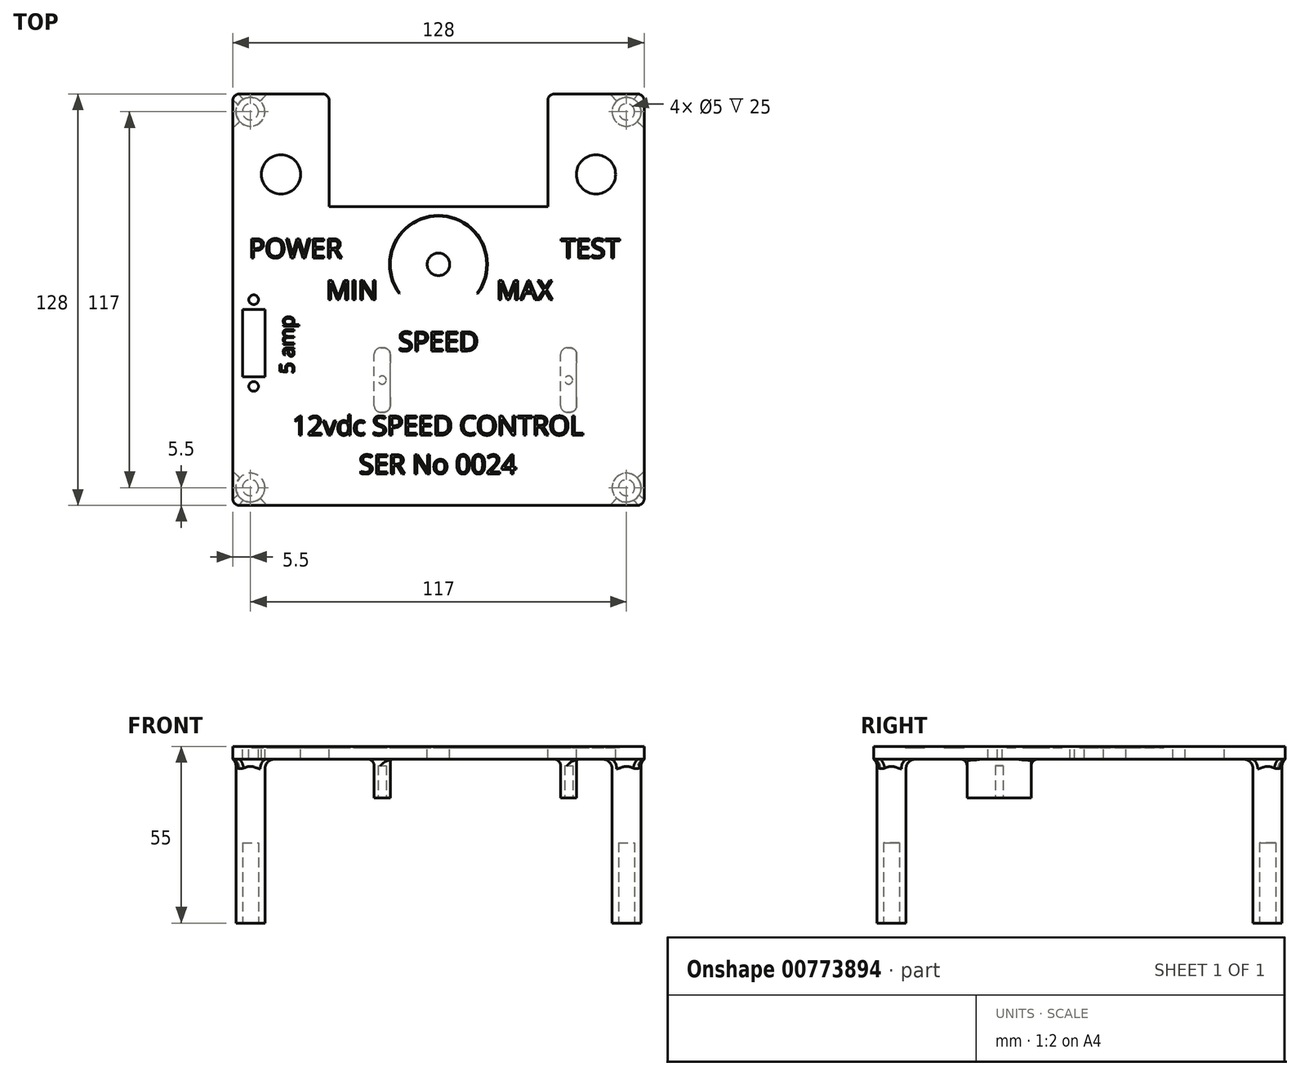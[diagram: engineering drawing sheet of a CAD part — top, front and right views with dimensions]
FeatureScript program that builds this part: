
annotation { "Feature Type Name" : "Feature", "Feature Type Description" : "" }
export const myFeature = defineFeature(function(context is Context, id is Id, definition is map)
    precondition{}
    {
        {
            var Q0;
            Q0=qCreatedBy(makeId("Top.planeOp"),FACE);
            var sketch = newSketch(context, id + "F0", { "sketchPlane" : qUnion([Q0])});
            skLineSegment(sketch, "E0.bottom", {"start": v(0, 0) * mm, "end": v(128, 0) * mm});
            skLineSegment(sketch, "E0.top", {"start": v(0, 128) * mm, "end": v(30, 128) * mm});
            skLineSegment(sketch, "E0.left", {"start": v(0, 0) * mm, "end": v(0, 128) * mm});
            skLineSegment(sketch, "E0.right", {"start": v(128, 0) * mm, "end": v(128, 128) * mm});
            skLineSegment(sketch, "E1", {"start": v(30, 128) * mm, "end": v(30, 93) * mm});
            skLineSegment(sketch, "E2", {"start": v(98, 93) * mm, "end": v(98, 128) * mm});
            skLineSegment(sketch, "E3", {"start": v(98, 93) * mm, "end": v(30, 93) * mm});
            skCircle(sketch, "E4", {"center": v(15, 103) * mm, "radius": 6.1 * mm});
            skCircle(sketch, "E5", {"center": v(113, 103) * mm, "radius": 6.1 * mm});
            skCircle(sketch, "E6", {"center": v(64, 75) * mm, "radius": 3.5 * mm});
            skLineSegment(sketch, "E7.bottom", {"start": v(3, 61) * mm, "end": v(10, 61) * mm});
            skLineSegment(sketch, "E7.top", {"start": v(3, 40) * mm, "end": v(10, 40) * mm});
            skLineSegment(sketch, "E7.left", {"start": v(3, 61) * mm, "end": v(3, 40) * mm});
            skLineSegment(sketch, "E7.right", {"start": v(10, 61) * mm, "end": v(10, 40) * mm});
            skLineSegment(sketch, "E8.trimOffspring", {"start": v(98, 128) * mm, "end": v(128, 128) * mm});
            skCircle(sketch, "E9", {"center": v(6.5, 64) * mm, "radius": 1.5 * mm});
            skPoint(sketch, "E9.centerSnap0", {"position": v(6.5, 61) * mm});
            skCircle(sketch, "E10", {"center": v(6.5, 37) * mm, "radius": 1.5 * mm});
            skPoint(sketch, "E10.centerSnap0", {"position": v(6.5, 40) * mm});
            skSolve(sketch);
        }
        {
            var Q0;
            Q0=makeQuery(id+"F0.imprint","IMPRINT",FACE,{"disambiguationData":[TD([[makeQuery(id+"F0.imprint","IMPRINT",EDGE,{"derivedFrom":sQuery(id+"F0.wireOp",EDGE,"E0.bottom")}),1.0]])]});
            extrude(context, id + "F1", {"entities" : qUnion([Q0]), "oppositeDirection" : true, "depth" : 4 * mm, "offsetDistance" : 25 * mm});
        }
        {
            var Q0;
            Q0=qCreatedBy(makeId("Top.planeOp"),FACE);
            var sketch = newSketch(context, id + "F2", { "sketchPlane" : qUnion([Q0])});
            skText(sketch, "E11", { "text": "SPEED", "fontName": "OpenSans-Regular.ttf"});
            skText(sketch, "E12", { "text": "POWER", "fontName": "OpenSans-Regular.ttf"});
            skText(sketch, "E13", { "text": "TEST", "fontName": "OpenSans-Regular.ttf"});
            skText(sketch, "E14", { "text": "MIN", "fontName": "OpenSans-Regular.ttf"});
            skText(sketch, "E15", { "text": "MAX", "fontName": "OpenSans-Regular.ttf"});
            skText(sketch, "E16", { "text": "5 amp\n", "fontName": "OpenSans-Regular.ttf"});
            skText(sketch, "E17", { "text": "12vdc SPEED CONTROL", "fontName": "OpenSans-Regular.ttf"});
            skArc(sketch, "E18", {"start": v(76, 66) * mm, "mid": v(64, 90) * mm, "end": v(52, 66) * mm});
            skArc(sketch, "E19", {"start": v(76.2, 65.86) * mm, "mid": v(64, 90.25) * mm, "end": v(51.8, 65.85) * mm});
            skLineSegment(sketch, "E20", {"start": v(52, 66) * mm, "end": v(51.8, 65.85) * mm});
            skLineSegment(sketch, "E21", {"start": v(76, 66) * mm, "end": v(76.2, 65.86) * mm});
            skText(sketch, "E22", { "text": "SER No 0024", "fontName": "OpenSans-Regular.ttf"});
            const initialGuessF2  = {"E11": [0.05152, 0.04806, 1, 0, 0.006], "E12": [0.005, 0.077, 1, 0, 0.006], "E13": [0.1021, 0.077, 1, 0, 0.006], "E14": [0.02907, 0.064, 1, 0, 0.006], "E15": [0.08194, 0.064, 1, 0, 0.006], "E16": [0.01905, 0.04095, 0, 1, 0.00444], "E17": [0.0185, 0.02184, 1, 0, 0.006], "E22": [0.03928, 0.0098, 1, 0, 0.006]};
            skSetInitialGuess(sketch, initialGuessF2);
            skSolve(sketch);
        }
        {
            var Q0;
            Q0 = qSketchRegion(id + "F2", true);
            extrude(context, id + "F3", {"entities" : qUnion([Q0]), "operationType" : NewBodyOperationType.REMOVE, "oppositeDirection" : true, "depth" : .5 * mm, "offsetDistance" : 25 * mm});
        }
        {
            var Q0;
            Q0=qCreatedBy(makeId("Top.planeOp"),FACE);
            var sketch = newSketch(context, id + "F4", { "sketchPlane" : qUnion([Q0])});
            skCircle(sketch, "E23", {"center": v(5.5, 122.5) * mm, "radius": 4.5 * mm});
            skCircle(sketch, "E24.1.0.0", {"center": v(122.5, 122.5) * mm, "radius": 4.5 * mm});
            skLineSegment(sketch, "E24.direction1", {"start": v(5.5, 122.5) * mm, "end": v(122.5, 122.5) * mm, "construction": true});
            skCircle(sketch, "E25", {"center": v(5.5, 5.5) * mm, "radius": 4.5 * mm});
            skCircle(sketch, "E26", {"center": v(122.5, 5.5) * mm, "radius": 4.5 * mm});
            skSolve(sketch);
        }
        {
            var Q0;
            Q0 = qSketchRegion(id + "F4", true);
            extrude(context, id + "F5", {"entities" : qUnion([Q0]), "operationType" : NewBodyOperationType.ADD, "oppositeDirection" : true, "depth" : 55 * mm, "offsetDistance" : 25 * mm});
        }
        {
            var Q0;
            Q0=makeQuery(id+"F5.opExtrude","CAP_FACE",FACE,{"disambiguationData":[OSD([sQuery(id+"F4.wireOp",EDGE,"E25")])],"isStart":false});
            var sketch = newSketch(context, id + "F6", { "sketchPlane" : qUnion([Q0])});
            skCircle(sketch, "E27", {"center": v(5.5, -5.5) * mm, "radius": 2.5 * mm});
            skCircle(sketch, "E28.0.1.0", {"center": v(5.5, -122.5) * mm, "radius": 2.5 * mm});
            skCircle(sketch, "E28.1.0.0", {"center": v(122.5, -5.5) * mm, "radius": 2.5 * mm});
            skCircle(sketch, "E28.1.1.0", {"center": v(122.5, -122.5) * mm, "radius": 2.5 * mm});
            skLineSegment(sketch, "E28.direction1", {"start": v(5.5, -5.5) * mm, "end": v(122.5, -5.5) * mm, "construction": true});
            skLineSegment(sketch, "E28.direction2", {"start": v(5.5, -5.5) * mm, "end": v(5.5, -122.5) * mm, "construction": true});
            skSolve(sketch);
        }
        {
            var Q0;
            Q0 = qSketchRegion(id + "F6", true);
            extrude(context, id + "F7", {"entities" : qUnion([Q0]), "operationType" : NewBodyOperationType.REMOVE, "oppositeDirection" : true, "depth" : 25 * mm, "offsetDistance" : 25 * mm});
        }
        {
            var Q0;
            Q0=makeQuery(id+"F1.opExtrude","SWEPT_EDGE",EDGE,{"disambiguationData":[OSD([sQuery(id+"F0.wireOp",EDGE,"E0.top"),sQuery(id+"F0.wireOp",EDGE,"E0.left")])]});
            var Q1;
            Q1=makeQuery(id+"F1.opExtrude","SWEPT_EDGE",EDGE,{"disambiguationData":[OSD([sQuery(id+"F0.wireOp",EDGE,"E0.right"),sQuery(id+"F0.wireOp",EDGE,"E8.trimOffspring")])]});
            var Q2;
            Q2=makeQuery(id+"F1.opExtrude","SWEPT_EDGE",EDGE,{"disambiguationData":[OSD([sQuery(id+"F0.wireOp",EDGE,"E0.bottom"),sQuery(id+"F0.wireOp",EDGE,"E0.right")])]});
            var Q3;
            Q3=makeQuery(id+"F1.opExtrude","SWEPT_EDGE",EDGE,{"disambiguationData":[OSD([sQuery(id+"F0.wireOp",EDGE,"E0.bottom"),sQuery(id+"F0.wireOp",EDGE,"E0.left")])]});
            var Q4;
            Q4=makeQuery(id+"F1.opExtrude","SWEPT_EDGE",EDGE,{"disambiguationData":[OSD([sQuery(id+"F0.wireOp",EDGE,"E0.top"),sQuery(id+"F0.wireOp",EDGE,"E1")])]});
            var Q5;
            Q5=makeQuery(id+"F1.opExtrude","SWEPT_EDGE",EDGE,{"disambiguationData":[OSD([sQuery(id+"F0.wireOp",EDGE,"E2"),sQuery(id+"F0.wireOp",EDGE,"E8.trimOffspring")])]});
            fillet(context, id + "F8", {"entities" : qUnion([Q0, Q1, Q2, Q3, Q4, Q5]), "radius" : 2 * mm, "tangentPropagation" : true, "allowEdgeOverflow" : false});
        }
        {
            var Q0;
            Q0=qCreatedBy(makeId("Top.planeOp"),FACE);
            var sketch = newSketch(context, id + "F9", { "sketchPlane" : qUnion([Q0])});
            skLineSegment(sketch, "E29.bottom", {"start": v(102, 29) * mm, "end": v(107, 29) * mm});
            skLineSegment(sketch, "E29.top", {"start": v(102, 49) * mm, "end": v(107, 49) * mm});
            skLineSegment(sketch, "E29.left", {"start": v(102, 29) * mm, "end": v(102, 49) * mm});
            skLineSegment(sketch, "E29.right", {"start": v(107, 29) * mm, "end": v(107, 49) * mm});
            skPoint(sketch, "E30.oppositeSnap0", {"position": v(104.5, 49) * mm});
            skLineSegment(sketch, "E30.bottom", {"start": v(44, 29) * mm, "end": v(49, 29) * mm});
            skLineSegment(sketch, "E30.top", {"start": v(44, 49) * mm, "end": v(49, 49) * mm});
            skLineSegment(sketch, "E30.left", {"start": v(49, 29) * mm, "end": v(49, 49) * mm});
            skLineSegment(sketch, "E30.right", {"start": v(44, 29) * mm, "end": v(44, 49) * mm});
            skSolve(sketch);
        }
        {
            var Q0;
            Q0 = qSketchRegion(id + "F9", true);
            extrude(context, id + "F10", {"entities" : qUnion([Q0]), "operationType" : NewBodyOperationType.ADD, "oppositeDirection" : true, "depth" : 16 * mm, "offsetDistance" : 25 * mm});
        }
        {
            var Q0;
            Q0=makeQuery(id+"F10.opExtrude","CAP_FACE",FACE,{"disambiguationData":[OSD([sQuery(id+"F9.wireOp",EDGE,"E29.bottom"),sQuery(id+"F9.wireOp",EDGE,"E29.top"),sQuery(id+"F9.wireOp",EDGE,"E29.left"),sQuery(id+"F9.wireOp",EDGE,"E29.right")])],"isStart":false});
            var sketch = newSketch(context, id + "F11", { "sketchPlane" : qUnion([Q0])});
            skCircle(sketch, "E31", {"center": v(104.5, -39) * mm, "radius": 1.25 * mm});
            skCircle(sketch, "E32", {"center": v(46.5, -39) * mm, "radius": 1.25 * mm});
            skPoint(sketch, "E33.orphan", {"position": v(104.5, -29) * mm});
            skPoint(sketch, "E34.orphan", {"position": v(104.5, -49) * mm});
            skSolve(sketch);
        }
        {
            var Q0;
            Q0 = qSketchRegion(id + "F11", true);
            extrude(context, id + "F12", {"entities" : qUnion([Q0]), "operationType" : NewBodyOperationType.REMOVE, "oppositeDirection" : true, "depth" : 10 * mm, "offsetDistance" : 25 * mm});
        }
        {
            var Q0;
            Q0=makeQuery(id+"F10.opExtrude","SWEPT_EDGE",EDGE,{"disambiguationData":[OSD([sQuery(id+"F9.wireOp",EDGE,"E30.bottom"),sQuery(id+"F9.wireOp",EDGE,"E30.left")])]});
            var Q1;
            Q1=makeQuery(id+"F10.opExtrude","SWEPT_EDGE",EDGE,{"disambiguationData":[OSD([sQuery(id+"F9.wireOp",EDGE,"E30.bottom"),sQuery(id+"F9.wireOp",EDGE,"E30.right")])]});
            var Q2;
            Q2=makeQuery(id+"F10.opExtrude","SWEPT_EDGE",EDGE,{"disambiguationData":[OSD([sQuery(id+"F9.wireOp",EDGE,"E29.bottom"),sQuery(id+"F9.wireOp",EDGE,"E29.right")])]});
            var Q3;
            Q3=makeQuery(id+"F10.opExtrude","SWEPT_EDGE",EDGE,{"disambiguationData":[OSD([sQuery(id+"F9.wireOp",EDGE,"E29.top"),sQuery(id+"F9.wireOp",EDGE,"E29.right")])]});
            var Q4;
            Q4=makeQuery(id+"F10.opExtrude","SWEPT_EDGE",EDGE,{"disambiguationData":[OSD([sQuery(id+"F9.wireOp",EDGE,"E29.bottom"),sQuery(id+"F9.wireOp",EDGE,"E29.left")])]});
            var Q5;
            Q5=makeQuery(id+"F10.opExtrude","SWEPT_EDGE",EDGE,{"disambiguationData":[OSD([sQuery(id+"F9.wireOp",EDGE,"E30.top"),sQuery(id+"F9.wireOp",EDGE,"E30.right")])]});
            var Q6;
            Q6=makeQuery(id+"F10.opExtrude","SWEPT_EDGE",EDGE,{"disambiguationData":[OSD([sQuery(id+"F9.wireOp",EDGE,"E29.top"),sQuery(id+"F9.wireOp",EDGE,"E29.left")])]});
            var Q7;
            Q7=makeQuery(id+"F10.opExtrude","SWEPT_EDGE",EDGE,{"disambiguationData":[OSD([sQuery(id+"F9.wireOp",EDGE,"E30.top"),sQuery(id+"F9.wireOp",EDGE,"E30.left")])]});
            var Q8;
            Q8=makeQuery(id+"F10.boolean.opBoolean","INTERSECT",EDGE,{"derivedFrom":[makeQuery(id+"F1.opExtrude","CAP_FACE",FACE,{"disambiguationData":[OSD([sQuery(id+"F0.wireOp",EDGE,"E0.bottom"),sQuery(id+"F0.wireOp",EDGE,"E0.top"),sQuery(id+"F0.wireOp",EDGE,"E0.left"),sQuery(id+"F0.wireOp",EDGE,"E0.right"),sQuery(id+"F0.wireOp",EDGE,"E1"),sQuery(id+"F0.wireOp",EDGE,"E2"),sQuery(id+"F0.wireOp",EDGE,"E3"),sQuery(id+"F0.wireOp",EDGE,"E4"),sQuery(id+"F0.wireOp",EDGE,"E5"),sQuery(id+"F0.wireOp",EDGE,"E6"),sQuery(id+"F0.wireOp",EDGE,"E7.bottom"),sQuery(id+"F0.wireOp",EDGE,"E7.top"),sQuery(id+"F0.wireOp",EDGE,"E7.left"),sQuery(id+"F0.wireOp",EDGE,"E7.right"),sQuery(id+"F0.wireOp",EDGE,"E8.trimOffspring"),sQuery(id+"F0.wireOp",EDGE,"E9"),sQuery(id+"F0.wireOp",EDGE,"E10")])],"isStart":false}),makeQuery(id+"F10.opExtrude","SWEPT_FACE",FACE,{"disambiguationData":[OSD([sQuery(id+"F9.wireOp",EDGE,"E30.right")])]})]});
            var Q9;
            Q9=makeQuery(id+"F10.boolean.opBoolean","INTERSECT",EDGE,{"derivedFrom":[makeQuery(id+"F1.opExtrude","CAP_FACE",FACE,{"disambiguationData":[OSD([sQuery(id+"F0.wireOp",EDGE,"E0.bottom"),sQuery(id+"F0.wireOp",EDGE,"E0.top"),sQuery(id+"F0.wireOp",EDGE,"E0.left"),sQuery(id+"F0.wireOp",EDGE,"E0.right"),sQuery(id+"F0.wireOp",EDGE,"E1"),sQuery(id+"F0.wireOp",EDGE,"E2"),sQuery(id+"F0.wireOp",EDGE,"E3"),sQuery(id+"F0.wireOp",EDGE,"E4"),sQuery(id+"F0.wireOp",EDGE,"E5"),sQuery(id+"F0.wireOp",EDGE,"E6"),sQuery(id+"F0.wireOp",EDGE,"E7.bottom"),sQuery(id+"F0.wireOp",EDGE,"E7.top"),sQuery(id+"F0.wireOp",EDGE,"E7.left"),sQuery(id+"F0.wireOp",EDGE,"E7.right"),sQuery(id+"F0.wireOp",EDGE,"E8.trimOffspring"),sQuery(id+"F0.wireOp",EDGE,"E9"),sQuery(id+"F0.wireOp",EDGE,"E10")])],"isStart":false}),makeQuery(id+"F10.opExtrude","SWEPT_FACE",FACE,{"disambiguationData":[OSD([sQuery(id+"F9.wireOp",EDGE,"E29.left")])]})]});
            fillet(context, id + "F13", {"entities" : qUnion([Q0, Q1, Q2, Q3, Q4, Q5, Q6, Q7, Q8, Q9]), "radius" : 2 * mm, "tangentPropagation" : true, "allowEdgeOverflow" : false});
        }
        {
            var Q0;
            Q0=makeQuery(id+"F5.boolean.opBoolean","INTERSECT",EDGE,{"derivedFrom":[makeQuery(id+"F1.opExtrude","CAP_FACE",FACE,{"disambiguationData":[OSD([sQuery(id+"F0.wireOp",EDGE,"E0.bottom"),sQuery(id+"F0.wireOp",EDGE,"E0.top"),sQuery(id+"F0.wireOp",EDGE,"E0.left"),sQuery(id+"F0.wireOp",EDGE,"E0.right"),sQuery(id+"F0.wireOp",EDGE,"E1"),sQuery(id+"F0.wireOp",EDGE,"E2"),sQuery(id+"F0.wireOp",EDGE,"E3"),sQuery(id+"F0.wireOp",EDGE,"E4"),sQuery(id+"F0.wireOp",EDGE,"E5"),sQuery(id+"F0.wireOp",EDGE,"E6"),sQuery(id+"F0.wireOp",EDGE,"E7.bottom"),sQuery(id+"F0.wireOp",EDGE,"E7.top"),sQuery(id+"F0.wireOp",EDGE,"E7.left"),sQuery(id+"F0.wireOp",EDGE,"E7.right"),sQuery(id+"F0.wireOp",EDGE,"E8.trimOffspring"),sQuery(id+"F0.wireOp",EDGE,"E9"),sQuery(id+"F0.wireOp",EDGE,"E10")])],"isStart":false}),makeQuery(id+"F5.opExtrude","SWEPT_FACE",FACE,{"disambiguationData":[OSD([sQuery(id+"F4.wireOp",EDGE,"E26")])]})]});
            var Q1;
            Q1=makeQuery(id+"F5.boolean.opBoolean","INTERSECT",EDGE,{"derivedFrom":[makeQuery(id+"F1.opExtrude","CAP_FACE",FACE,{"disambiguationData":[OSD([sQuery(id+"F0.wireOp",EDGE,"E0.bottom"),sQuery(id+"F0.wireOp",EDGE,"E0.top"),sQuery(id+"F0.wireOp",EDGE,"E0.left"),sQuery(id+"F0.wireOp",EDGE,"E0.right"),sQuery(id+"F0.wireOp",EDGE,"E1"),sQuery(id+"F0.wireOp",EDGE,"E2"),sQuery(id+"F0.wireOp",EDGE,"E3"),sQuery(id+"F0.wireOp",EDGE,"E4"),sQuery(id+"F0.wireOp",EDGE,"E5"),sQuery(id+"F0.wireOp",EDGE,"E6"),sQuery(id+"F0.wireOp",EDGE,"E7.bottom"),sQuery(id+"F0.wireOp",EDGE,"E7.top"),sQuery(id+"F0.wireOp",EDGE,"E7.left"),sQuery(id+"F0.wireOp",EDGE,"E7.right"),sQuery(id+"F0.wireOp",EDGE,"E8.trimOffspring"),sQuery(id+"F0.wireOp",EDGE,"E9"),sQuery(id+"F0.wireOp",EDGE,"E10")])],"isStart":false}),makeQuery(id+"F5.opExtrude","SWEPT_FACE",FACE,{"disambiguationData":[OSD([sQuery(id+"F4.wireOp",EDGE,"E25")])]})]});
            var Q2;
            Q2=makeQuery(id+"F5.boolean.opBoolean","INTERSECT",EDGE,{"derivedFrom":[makeQuery(id+"F1.opExtrude","CAP_FACE",FACE,{"disambiguationData":[OSD([sQuery(id+"F0.wireOp",EDGE,"E0.bottom"),sQuery(id+"F0.wireOp",EDGE,"E0.top"),sQuery(id+"F0.wireOp",EDGE,"E0.left"),sQuery(id+"F0.wireOp",EDGE,"E0.right"),sQuery(id+"F0.wireOp",EDGE,"E1"),sQuery(id+"F0.wireOp",EDGE,"E2"),sQuery(id+"F0.wireOp",EDGE,"E3"),sQuery(id+"F0.wireOp",EDGE,"E4"),sQuery(id+"F0.wireOp",EDGE,"E5"),sQuery(id+"F0.wireOp",EDGE,"E6"),sQuery(id+"F0.wireOp",EDGE,"E7.bottom"),sQuery(id+"F0.wireOp",EDGE,"E7.top"),sQuery(id+"F0.wireOp",EDGE,"E7.left"),sQuery(id+"F0.wireOp",EDGE,"E7.right"),sQuery(id+"F0.wireOp",EDGE,"E8.trimOffspring"),sQuery(id+"F0.wireOp",EDGE,"E9"),sQuery(id+"F0.wireOp",EDGE,"E10")])],"isStart":false}),makeQuery(id+"F5.opExtrude","SWEPT_FACE",FACE,{"disambiguationData":[OSD([sQuery(id+"F4.wireOp",EDGE,"E23")])]})]});
            var Q3;
            Q3=makeQuery(id+"F5.boolean.opBoolean","INTERSECT",EDGE,{"derivedFrom":[makeQuery(id+"F1.opExtrude","CAP_FACE",FACE,{"disambiguationData":[OSD([sQuery(id+"F0.wireOp",EDGE,"E0.bottom"),sQuery(id+"F0.wireOp",EDGE,"E0.top"),sQuery(id+"F0.wireOp",EDGE,"E0.left"),sQuery(id+"F0.wireOp",EDGE,"E0.right"),sQuery(id+"F0.wireOp",EDGE,"E1"),sQuery(id+"F0.wireOp",EDGE,"E2"),sQuery(id+"F0.wireOp",EDGE,"E3"),sQuery(id+"F0.wireOp",EDGE,"E4"),sQuery(id+"F0.wireOp",EDGE,"E5"),sQuery(id+"F0.wireOp",EDGE,"E6"),sQuery(id+"F0.wireOp",EDGE,"E7.bottom"),sQuery(id+"F0.wireOp",EDGE,"E7.top"),sQuery(id+"F0.wireOp",EDGE,"E7.left"),sQuery(id+"F0.wireOp",EDGE,"E7.right"),sQuery(id+"F0.wireOp",EDGE,"E8.trimOffspring"),sQuery(id+"F0.wireOp",EDGE,"E9"),sQuery(id+"F0.wireOp",EDGE,"E10")])],"isStart":false}),makeQuery(id+"F5.opExtrude","SWEPT_FACE",FACE,{"disambiguationData":[OSD([sQuery(id+"F4.wireOp",EDGE,"E24.1.0.0")])]})]});
            fillet(context, id + "F14", {"entities" : qUnion([Q0, Q1, Q2, Q3]), "radius" : 3 * mm, "tangentPropagation" : true, "allowEdgeOverflow" : false});
        }
    });
